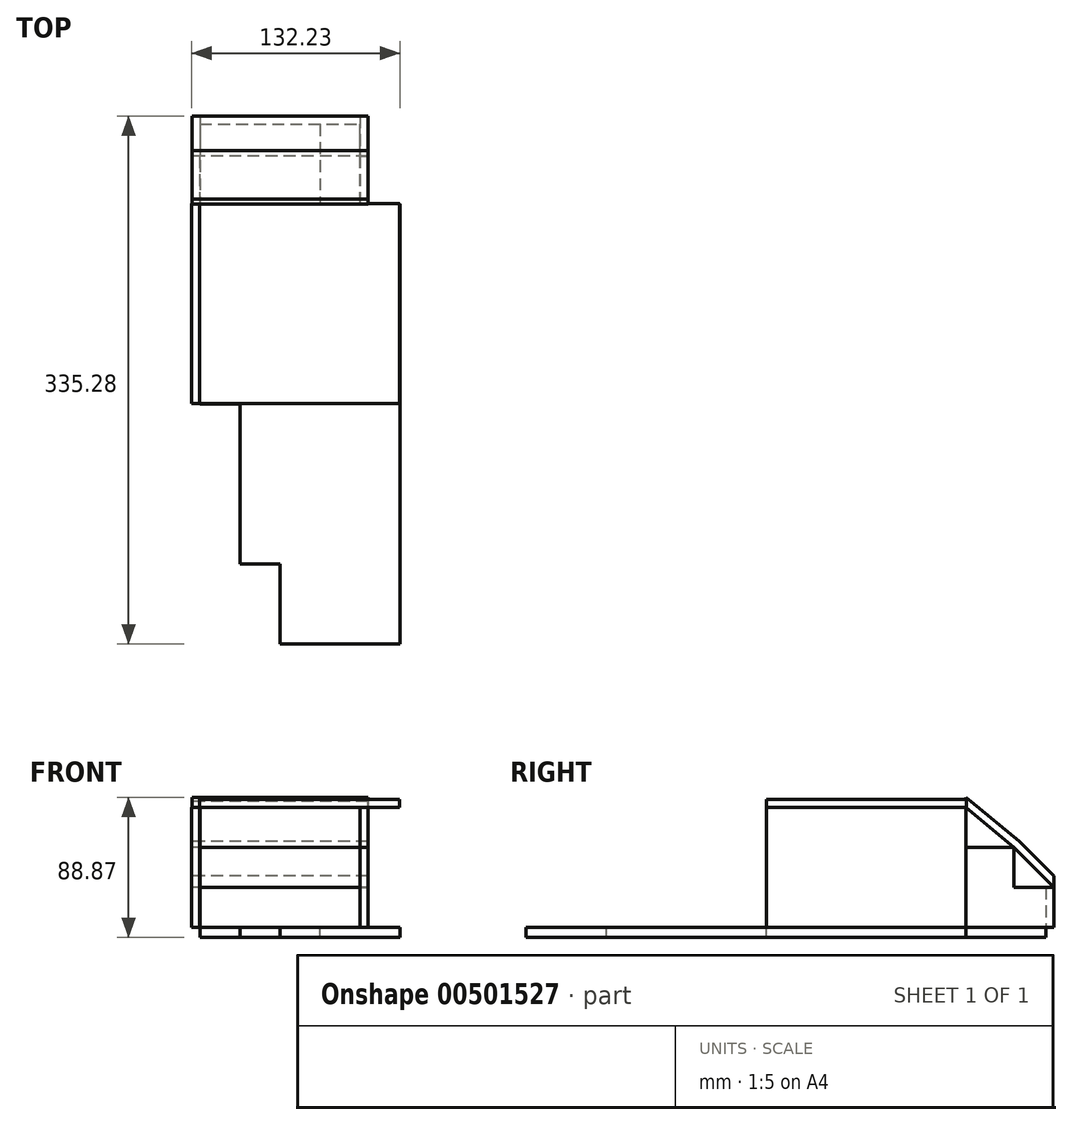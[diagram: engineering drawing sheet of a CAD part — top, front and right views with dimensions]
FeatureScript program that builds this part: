
annotation { "Feature Type Name" : "Feature", "Feature Type Description" : "" }
export const myFeature = defineFeature(function(context is Context, id is Id, definition is map)
    precondition{}
    {
        {
            var Q0;
            Q0=qCreatedBy(makeId("Top.planeOp"),FACE);
            var sketch = newSketch(context, id + "F0", { "sketchPlane" : qUnion([Q0])});
            skLineSegment(sketch, "E0.left", {"start": v(-63.5, 63.5) * mm, "end": v(-63.5, -63.5) * mm});
            skLineSegment(sketch, "E0.right", {"start": v(63.5, 63.5) * mm, "end": v(63.5, -63.5) * mm});
            skPoint(sketch, "E0.middle", {"position": v(0, 0) * mm});
            skLineSegment(sketch, "E1.top", {"start": v(-63.5, 38.1) * mm, "end": v(-38.1, 38.1) * mm, "construction": true});
            skLineSegment(sketch, "E1.left", {"start": v(-63.5, 63.5) * mm, "end": v(-63.5, 38.1) * mm, "construction": true});
            skLineSegment(sketch, "E1.right", {"start": v(-38.1, 63.5) * mm, "end": v(-38.1, 38.1) * mm, "construction": true});
            skLineSegment(sketch, "E2.0", {"start": v(-12.7, 63.5) * mm, "end": v(-12.7, 38.1) * mm, "construction": true});
            skLineSegment(sketch, "E3.0", {"start": v(12.7, 63.5) * mm, "end": v(12.7, 38.1) * mm, "construction": true});
            skLineSegment(sketch, "E4.0", {"start": v(38.1, 63.5) * mm, "end": v(38.1, 38.1) * mm, "construction": true});
            skLineSegment(sketch, "E5", {"start": v(-38.1, 38.1) * mm, "end": v(-12.7, 38.1) * mm, "construction": true});
            skLineSegment(sketch, "E6", {"start": v(12.7, 38.1) * mm, "end": v(-12.7, 38.1) * mm, "construction": true});
            skLineSegment(sketch, "E7", {"start": v(12.7, 38.1) * mm, "end": v(38.1, 38.1) * mm, "construction": true});
            skLineSegment(sketch, "E8", {"start": v(38.1, 38.1) * mm, "end": v(63.5, 38.1) * mm, "construction": true});
            skLineSegment(sketch, "E9.0", {"start": v(38.1, 12.7) * mm, "end": v(63.5, 12.7) * mm, "construction": true});
            skLineSegment(sketch, "E10.0", {"start": v(38.1, -12.7) * mm, "end": v(63.5, -12.7) * mm, "construction": true});
            skLineSegment(sketch, "E11.0", {"start": v(38.1, -38.1) * mm, "end": v(63.5, -38.1) * mm, "construction": true});
            skLineSegment(sketch, "E12.0", {"start": v(38.1, -63.5) * mm, "end": v(63.5, -63.5) * mm, "construction": true});
            skLineSegment(sketch, "E13", {"start": v(38.1, -63.5) * mm, "end": v(38.1, -38.1) * mm, "construction": true});
            skLineSegment(sketch, "E14", {"start": v(38.1, -12.7) * mm, "end": v(38.1, -38.1) * mm, "construction": true});
            skLineSegment(sketch, "E15", {"start": v(38.1, -12.7) * mm, "end": v(38.1, 12.7) * mm, "construction": true});
            skLineSegment(sketch, "E16", {"start": v(38.1, 38.1) * mm, "end": v(38.1, 12.7) * mm, "construction": true});
            skLineSegment(sketch, "E17.0", {"start": v(-63.5, 88.9) * mm, "end": v(-38.1, 88.9) * mm, "construction": true});
            skLineSegment(sketch, "E18.0", {"start": v(-63.5, 114.3) * mm, "end": v(-38.1, 114.3) * mm});
            skLineSegment(sketch, "E19", {"start": v(-63.5, 114.3) * mm, "end": v(-63.5, 63.5) * mm});
            skLineSegment(sketch, "E20", {"start": v(38.1, 63.5) * mm, "end": v(38.1, 88.9) * mm});
            skLineSegment(sketch, "E21", {"start": v(38.1, 88.9) * mm, "end": v(-38.1, 88.9) * mm, "construction": true});
            skLineSegment(sketch, "E22", {"start": v(-38.1, 114.3) * mm, "end": v(-38.1, 88.9) * mm, "construction": true});
            skLineSegment(sketch, "E23", {"start": v(-38.1, 63.5) * mm, "end": v(-38.1, 88.9) * mm, "construction": true});
            skLineSegment(sketch, "E24", {"start": v(38.1, 88.9) * mm, "end": v(38.1, 114.3) * mm});
            skLineSegment(sketch, "E25", {"start": v(38.1, 114.3) * mm, "end": v(-38.1, 114.3) * mm});
            skLineSegment(sketch, "E26.0", {"start": v(-12.7, 114.3) * mm, "end": v(-12.7, 88.9) * mm, "construction": true});
            skLineSegment(sketch, "E27.0", {"start": v(12.7, 114.3) * mm, "end": v(12.7, 88.9) * mm, "construction": true});
            skLineSegment(sketch, "E28.0", {"start": v(-12.7, 63.5) * mm, "end": v(-12.7, 88.9) * mm, "construction": true});
            skLineSegment(sketch, "E29.0", {"start": v(12.7, 63.5) * mm, "end": v(12.7, 88.9) * mm, "construction": true});
            skLineSegment(sketch, "E30.0", {"start": v(12.7, -63.5) * mm, "end": v(12.7, -38.1) * mm, "construction": true});
            skLineSegment(sketch, "E31.0", {"start": v(-12.7, -63.5) * mm, "end": v(-12.7, -38.1) * mm, "construction": true});
            skLineSegment(sketch, "E32.0", {"start": v(-38.1, -63.5) * mm, "end": v(-38.1, -38.1) * mm, "construction": true});
            skLineSegment(sketch, "E33", {"start": v(-63.5, -38.1) * mm, "end": v(-38.1, -38.1) * mm, "construction": true});
            skLineSegment(sketch, "E34", {"start": v(-12.7, -38.1) * mm, "end": v(38.1, -38.1) * mm, "construction": true});
            skLineSegment(sketch, "E35", {"start": v(-12.7, -38.1) * mm, "end": v(-38.1, -38.1) * mm, "construction": true});
            skLineSegment(sketch, "E36", {"start": v(-38.1, -63.5) * mm, "end": v(-38.1, -88.9) * mm});
            skLineSegment(sketch, "E37", {"start": v(-38.1, -88.9) * mm, "end": v(63.5, -88.9) * mm, "construction": true});
            skLineSegment(sketch, "E38", {"start": v(63.5, -88.9) * mm, "end": v(63.5, -63.5) * mm});
            skLineSegment(sketch, "E39", {"start": v(38.1, -63.5) * mm, "end": v(38.1, -88.9) * mm, "construction": true});
            skLineSegment(sketch, "E40", {"start": v(12.7, -63.5) * mm, "end": v(12.7, -88.9) * mm});
            skLineSegment(sketch, "E41", {"start": v(-12.7, -63.5) * mm, "end": v(-12.7, -88.9) * mm});
            skLineSegment(sketch, "E42", {"start": v(-38.1, -88.9) * mm, "end": v(-38.1, -165.1) * mm});
            skLineSegment(sketch, "E43", {"start": v(-38.1, -165.1) * mm, "end": v(63.5, -165.1) * mm});
            skLineSegment(sketch, "E44", {"start": v(63.5, -165.1) * mm, "end": v(63.5, -88.9) * mm});
            skLineSegment(sketch, "E45", {"start": v(-38.1, -165.1) * mm, "end": v(-38.1, -139.7) * mm, "construction": true});
            skLineSegment(sketch, "E46", {"start": v(-38.1, -139.7) * mm, "end": v(63.5, -139.7) * mm, "construction": true});
            skLineSegment(sketch, "E47", {"start": v(38.1, -88.9) * mm, "end": v(38.1, -165.1) * mm, "construction": true});
            skLineSegment(sketch, "E48", {"start": v(12.7, -88.9) * mm, "end": v(12.7, -165.1) * mm, "construction": true});
            skLineSegment(sketch, "E49", {"start": v(-12.7, -91.63) * mm, "end": v(-12.7, -165.1) * mm, "construction": true});
            skLineSegment(sketch, "E50", {"start": v(-38.1, -88.9) * mm, "end": v(-38.1, -114.3) * mm});
            skLineSegment(sketch, "E51", {"start": v(63.5, -114.3) * mm, "end": v(-38.1, -114.3) * mm, "construction": true});
            skLineSegment(sketch, "E52", {"start": v(-12.7, -165.1) * mm, "end": v(-12.7, -190.5) * mm});
            skLineSegment(sketch, "E53", {"start": v(-12.7, -190.5) * mm, "end": v(-12.7, -215.9) * mm});
            skLineSegment(sketch, "E54", {"start": v(-12.7, -215.9) * mm, "end": v(63.5, -215.9) * mm});
            skLineSegment(sketch, "E55", {"start": v(63.5, -215.9) * mm, "end": v(63.5, -165.1) * mm});
            skLineSegment(sketch, "E56", {"start": v(38.1, -165.1) * mm, "end": v(38.1, -215.9) * mm, "construction": true});
            skLineSegment(sketch, "E57", {"start": v(12.7, -165.1) * mm, "end": v(12.7, -215.9) * mm, "construction": true});
            skLineSegment(sketch, "E58", {"start": v(-12.7, -190.5) * mm, "end": v(63.5, -190.5) * mm, "construction": true});
            skLineSegment(sketch, "E59", {"start": v(12.7, 38.1) * mm, "end": v(12.7, -38.1) * mm, "construction": true});
            skLineSegment(sketch, "E60", {"start": v(-12.7, -38.1) * mm, "end": v(-12.7, 38.1) * mm, "construction": true});
            skLineSegment(sketch, "E61", {"start": v(-38.1, 38.1) * mm, "end": v(-38.1, -38.1) * mm, "construction": true});
            skLineSegment(sketch, "E62", {"start": v(38.1, -12.7) * mm, "end": v(-63.5, -12.7) * mm, "construction": true});
            skLineSegment(sketch, "E63", {"start": v(38.1, 12.7) * mm, "end": v(-63.5, 12.7) * mm, "construction": true});
            skLineSegment(sketch, "E64", {"start": v(-63.5, 63.5) * mm, "end": v(38.1, 63.5) * mm});
            skLineSegment(sketch, "E65", {"start": v(38.1, 63.5) * mm, "end": v(63.5, 63.5) * mm});
            skLineSegment(sketch, "E66", {"start": v(-63.5, -63.5) * mm, "end": v(63.5, -63.5) * mm});
            skSolve(sketch);
        }
        {
            var Q0;
            Q0=makeQuery(id+"F0.imprint","IMPRINT",FACE,{"disambiguationData":[TD([[makeQuery(id+"F0.imprint","IMPRINT",EDGE,{"derivedFrom":sQuery(id+"F0.wireOp",EDGE,"E18.0")}),-1.0]])]});
            extrude(context, id + "F1", {"entities" : qUnion([Q0]), "depth" : 6.35 * mm});
        }
        {
            var Q0;
            {var subQ3=sQuery(id+"F0.wireOp",EDGE,"E0.left");Q0=makeQuery(id+"F0.imprint","IMPRINT",FACE,{"disambiguationData":[TD([[makeQuery(id+"F0.imprint","IMPRINT",EDGE,{"derivedFrom":subQ3}),1.0]])]});}
            extrude(context, id + "F2", {"entities" : qUnion([Q0]), "operationType" : NewBodyOperationType.ADD, "depth" : 6.35 * mm});
        }
        {
            var Q0;
            {var subQ4=sQuery(id+"F0.wireOp",EDGE,"E36");Q0=makeQuery(id+"F0.imprint","IMPRINT",FACE,{"disambiguationData":[TD([[makeQuery(id+"F0.imprint","IMPRINT",EDGE,{"derivedFrom":subQ4}),1.0]])]});}
            extrude(context, id + "F3", {"entities" : qUnion([Q0]), "operationType" : NewBodyOperationType.ADD, "depth" : 6.35 * mm});
        }
        {
            var Q0;
            {var subQ0=sQuery(id+"F0.wireOp",EDGE,"E52");Q0=makeQuery(id+"F0.imprint","IMPRINT",FACE,{"disambiguationData":[TD([[makeQuery(id+"F0.imprint","IMPRINT",EDGE,{"derivedFrom":subQ0}),1.0]])]});}
            extrude(context, id + "F4", {"entities" : qUnion([Q0]), "operationType" : NewBodyOperationType.ADD, "depth" : 6.35 * mm});
        }
        {
            var Q0;
            {var subQ0=sQuery(id+"F0.wireOp",EDGE,"E43");var subQ1=sQuery(id+"F0.wireOp",EDGE,"E66");var subQ2=sQuery(id+"F0.wireOp",EDGE,"E64");Q0=makeQuery(id+"F4.boolean.opBoolean","MERGE",FACE,{"derivedFrom":[makeQuery(id+"F3.boolean.opBoolean","MERGE",FACE,{"derivedFrom":[makeQuery(id+"F2.boolean.opBoolean","MERGE",FACE,{"derivedFrom":[makeQuery(id+"F1.opExtrude","CAP_FACE",FACE,{"disambiguationData":[OSD([sQuery(id+"F0.wireOp",EDGE,"E18.0"),sQuery(id+"F0.wireOp",EDGE,"E19"),sQuery(id+"F0.wireOp",EDGE,"E20"),sQuery(id+"F0.wireOp",EDGE,"E24"),sQuery(id+"F0.wireOp",EDGE,"E25"),subQ2])],"isStart":false}),makeQuery(id+"F2.opExtrude","CAP_FACE",FACE,{"disambiguationData":[OSD([sQuery(id+"F0.wireOp",EDGE,"E0.left"),sQuery(id+"F0.wireOp",EDGE,"E0.right"),subQ2,sQuery(id+"F0.wireOp",EDGE,"E65"),subQ1])],"isStart":false})]}),makeQuery(id+"F3.opExtrude","CAP_FACE",FACE,{"disambiguationData":[OSD([sQuery(id+"F0.wireOp",EDGE,"E36"),sQuery(id+"F0.wireOp",EDGE,"E38"),sQuery(id+"F0.wireOp",EDGE,"E42"),subQ0,sQuery(id+"F0.wireOp",EDGE,"E44"),sQuery(id+"F0.wireOp",EDGE,"E50"),subQ1])],"isStart":false})]}),makeQuery(id+"F4.opExtrude","CAP_FACE",FACE,{"disambiguationData":[OSD([subQ0,sQuery(id+"F0.wireOp",EDGE,"E52"),sQuery(id+"F0.wireOp",EDGE,"E53"),sQuery(id+"F0.wireOp",EDGE,"E54"),sQuery(id+"F0.wireOp",EDGE,"E55")])],"isStart":false})]});}
            var sketch = newSketch(context, id + "F5", { "sketchPlane" : qUnion([Q0])});
            skLineSegment(sketch, "E67", {"start": v(-63.5, 114.3) * mm, "end": v(38.1, 114.3) * mm});
            skLineSegment(sketch, "E68", {"start": v(38.1, 114.3) * mm, "end": v(38.1, 63.5) * mm});
            skLineSegment(sketch, "E69", {"start": v(38.1, 63.5) * mm, "end": v(-63.5, 63.5) * mm});
            skLineSegment(sketch, "E70", {"start": v(-63.5, 63.5) * mm, "end": v(-63.5, 114.3) * mm});
            skLineSegment(sketch, "E71", {"start": v(38.1, 114.3) * mm, "end": v(12.7, 114.3) * mm, "construction": true});
            skLineSegment(sketch, "E72", {"start": v(12.7, 114.3) * mm, "end": v(12.7, 88.9) * mm});
            skLineSegment(sketch, "E73", {"start": v(12.7, 88.9) * mm, "end": v(12.7, 63.5) * mm});
            skLineSegment(sketch, "E74", {"start": v(12.7, 88.9) * mm, "end": v(38.1, 88.9) * mm});
            skLineSegment(sketch, "E75.0", {"start": v(43.18, 119.38) * mm, "end": v(43.18, 63.5) * mm});
            skLineSegment(sketch, "E75.1", {"start": v(-68.58, 119.38) * mm, "end": v(43.18, 119.38) * mm});
            skLineSegment(sketch, "E75.2", {"start": v(-68.58, 63.5) * mm, "end": v(-68.58, 119.38) * mm});
            skLineSegment(sketch, "E76", {"start": v(38.1, 63.5) * mm, "end": v(43.18, 63.5) * mm});
            skLineSegment(sketch, "E77", {"start": v(-63.5, 63.5) * mm, "end": v(-68.58, 63.5) * mm});
            skSolve(sketch);
        }
        {
            var Q0;
            {var subQ5=sQuery(id+"F5.wireOp",EDGE,"E70");Q0=makeQuery(id+"F5.imprint","IMPRINT",FACE,{"disambiguationData":[TD([[makeQuery(id+"F5.imprint","IMPRINT",EDGE,{"derivedFrom":subQ5}),-1.0]])]});}
            extrude(context, id + "F6", {"entities" : qUnion([Q0]), "depth" : 50.8 * mm});
        }
        {
            var Q0;
            {var subQ3=sQuery(id+"F5.wireOp",EDGE,"E72");Q0=makeQuery(id+"F5.imprint","IMPRINT",FACE,{"disambiguationData":[TD([[makeQuery(id+"F5.imprint","IMPRINT",EDGE,{"derivedFrom":subQ3}),1.0]])]});}
            var Q1;
            {var subQ4=sQuery(id+"F5.wireOp",EDGE,"E73");Q1=makeQuery(id+"F5.imprint","IMPRINT",FACE,{"disambiguationData":[TD([[makeQuery(id+"F5.imprint","IMPRINT",EDGE,{"derivedFrom":subQ4}),1.0]])]});}
            extrude(context, id + "F7", {"entities" : qUnion([Q0, Q1]), "operationType" : NewBodyOperationType.REMOVE, "oppositeDirection" : true, "depth" : 25.4 * mm});
        }
        {
            var Q0;
            {var subQ3=sQuery(id+"F5.wireOp",EDGE,"E76");Q0=makeQuery(id+"F5.imprint","IMPRINT",FACE,{"disambiguationData":[TD([[makeQuery(id+"F5.imprint","IMPRINT",EDGE,{"derivedFrom":subQ3}),-1.0]])]});}
            var sketch = newSketch(context, id + "F8", { "sketchPlane" : qUnion([Q0])});
            skLineSegment(sketch, "E78", {"start": v(-63.65, 63.74) * mm, "end": v(-63.65, -63.1) * mm});
            skLineSegment(sketch, "E79", {"start": v(-63.65, -63.1) * mm, "end": v(-38.28, -63.1) * mm});
            skLineSegment(sketch, "E80", {"start": v(-63.65, 63.74) * mm, "end": v(63.35, 63.74) * mm});
            skLineSegment(sketch, "E81", {"start": v(63.35, 63.74) * mm, "end": v(63.35, -63.26) * mm});
            skLineSegment(sketch, "E82", {"start": v(63.35, -63.26) * mm, "end": v(-38.28, -63.1) * mm});
            skLineSegment(sketch, "E83", {"start": v(37.95, 63.74) * mm, "end": v(63.35, 63.74) * mm});
            skLineSegment(sketch, "E84.0", {"start": v(-68.73, 63.74) * mm, "end": v(-68.73, -63.1) * mm});
            skLineSegment(sketch, "E85.0", {"start": v(68.43, 68.82) * mm, "end": v(68.43, -63.26) * mm});
            skLineSegment(sketch, "E85.1", {"start": v(43.03, 68.82) * mm, "end": v(68.43, 68.82) * mm});
            skLineSegment(sketch, "E86", {"start": v(37.95, 63.74) * mm, "end": v(37.95, 68.82) * mm});
            skLineSegment(sketch, "E87", {"start": v(37.95, 68.82) * mm, "end": v(43.03, 68.82) * mm});
            skLineSegment(sketch, "E88", {"start": v(-68.73, 63.74) * mm, "end": v(-63.65, 63.74) * mm});
            skLineSegment(sketch, "E89", {"start": v(-68.73, -63.1) * mm, "end": v(-63.65, -63.1) * mm});
            skLineSegment(sketch, "E90", {"start": v(63.35, -63.26) * mm, "end": v(68.43, -63.26) * mm});
            skSolve(sketch);
        }
        {
            var Q0;
            {var subQ0=sQuery(id+"F8.wireOp",EDGE,"E83");Q0=makeQuery(id+"F8.imprint","IMPRINT",FACE,{"disambiguationData":[TD([[makeQuery(id+"F8.imprint","IMPRINT",EDGE,{"derivedFrom":subQ0}),1.0]])]});}
            var Q1;
            Q1=makeQuery(id+"F8.imprint","IMPRINT",FACE,{"disambiguationData":[TD([[makeQuery(id+"F8.imprint","IMPRINT",EDGE,{"derivedFrom":sQuery(id+"F8.wireOp",EDGE,"E78")}),-1.0]])]});
            extrude(context, id + "F9", {"entities" : qUnion([Q0, Q1]), "depth" : 76.2 * mm});
        }
        {
            var Q0;
            Q0=makeQuery(id+"F6.opExtrude","SWEPT_FACE",FACE,{"disambiguationData":[OSD([sQuery(id+"F5.wireOp",EDGE,"E75.2")])]});
            var sketch = newSketch(context, id + "F10", { "sketchPlane" : qUnion([Q0])});
            skLineSegment(sketch, "E91", {"start": v(-119.38, 57.15) * mm, "end": v(-93.98, 57.15) * mm});
            skLineSegment(sketch, "E92", {"start": v(-93.98, 57.15) * mm, "end": v(-93.98, 31.75) * mm});
            skLineSegment(sketch, "E93", {"start": v(-93.98, 31.75) * mm, "end": v(-119.38, 31.75) * mm});
            skLineSegment(sketch, "E94", {"start": v(-119.38, 31.75) * mm, "end": v(-119.38, 57.15) * mm});
            skSolve(sketch);
        }
        {
            var Q0;
            Q0=makeQuery(id+"F10.imprint","IMPRINT",FACE,{"disambiguationData":[TD([[makeQuery(id+"F10.imprint","IMPRINT",EDGE,{"derivedFrom":sQuery(id+"F10.wireOp",EDGE,"E91")}),1.0]])]});
            extrude(context, id + "F11", {"entities" : qUnion([Q0]), "operationType" : NewBodyOperationType.REMOVE, "oppositeDirection" : true, "depth" : 114.3 * mm});
        }
        {
            var Q0;
            Q0=makeQuery(id+"F6.opExtrude","SWEPT_FACE",FACE,{"disambiguationData":[OSD([sQuery(id+"F5.wireOp",EDGE,"E75.2")])]});
            var sketch = newSketch(context, id + "F12", { "sketchPlane" : qUnion([Q0])});
            skLineSegment(sketch, "E95", {"start": v(-93.98, 57.15) * mm, "end": v(-63.5, 57.15) * mm});
            skLineSegment(sketch, "E96", {"start": v(-63.5, 57.15) * mm, "end": v(-63.5, 82.55) * mm});
            skLineSegment(sketch, "E97", {"start": v(-63.5, 82.55) * mm, "end": v(-93.98, 57.15) * mm});
            skLineSegment(sketch, "E98", {"start": v(-93.98, 57.15) * mm, "end": v(-93.98, 31.75) * mm});
            skLineSegment(sketch, "E99", {"start": v(-93.98, 31.75) * mm, "end": v(-119.38, 31.75) * mm});
            skLineSegment(sketch, "E100", {"start": v(-119.38, 31.75) * mm, "end": v(-93.98, 57.15) * mm});
            skLineSegment(sketch, "E101.0", {"start": v(-66.75, 86.45) * mm, "end": v(-97.4, 60.9) * mm});
            skLineSegment(sketch, "E101.1", {"start": v(-119.38, 38.93) * mm, "end": v(-97.4, 60.9) * mm});
            skLineSegment(sketch, "E102", {"start": v(-63.5, 82.55) * mm, "end": v(-63.5, 88.87) * mm});
            skLineSegment(sketch, "E103", {"start": v(-66.75, 86.45) * mm, "end": v(-63.5, 88.87) * mm});
            skLineSegment(sketch, "E104", {"start": v(-119.38, 31.75) * mm, "end": v(-119.38, 38.93) * mm});
            skSolve(sketch);
        }
        {
            var Q0;
            Q0=makeQuery(id+"F12.imprint","IMPRINT",FACE,{"disambiguationData":[TD([[makeQuery(id+"F12.imprint","IMPRINT",EDGE,{"derivedFrom":sQuery(id+"F12.wireOp",EDGE,"E98")}),-1.0]])]});
            var Q1;
            Q1=makeQuery(id+"F12.imprint","IMPRINT",FACE,{"disambiguationData":[TD([[makeQuery(id+"F12.imprint","IMPRINT",EDGE,{"derivedFrom":sQuery(id+"F12.wireOp",EDGE,"E95")}),-1.0]])]});
            extrude(context, id + "F13", {"entities" : qUnion([Q0, Q1]), "oppositeDirection" : true, "depth" : 5.08 * mm});
        }
        {
            var Q0;
            Q0=makeQuery(id+"F12.imprint","IMPRINT",FACE,{"disambiguationData":[TD([[makeQuery(id+"F12.imprint","IMPRINT",EDGE,{"derivedFrom":sQuery(id+"F12.wireOp",EDGE,"E97")}),-1.0]])]});
            extrude(context, id + "F14", {"entities" : qUnion([Q0]), "oppositeDirection" : true, "depth" : 111.76 * mm});
        }
        {
            var Q0;
            Q0=makeQuery(id+"F6.opExtrude","SWEPT_FACE",FACE,{"disambiguationData":[OSD([sQuery(id+"F5.wireOp",EDGE,"E75.0")])]});
            var sketch = newSketch(context, id + "F15", { "sketchPlane" : qUnion([Q0])});
            skLineSegment(sketch, "E105", {"start": v(93.98, 57.15) * mm, "end": v(63.5, 57.15) * mm});
            skLineSegment(sketch, "E106", {"start": v(63.5, 57.15) * mm, "end": v(63.5, 82.55) * mm});
            skLineSegment(sketch, "E107", {"start": v(63.5, 82.55) * mm, "end": v(93.98, 57.15) * mm});
            skLineSegment(sketch, "E108", {"start": v(93.98, 57.15) * mm, "end": v(93.98, 31.75) * mm});
            skLineSegment(sketch, "E109", {"start": v(93.98, 31.75) * mm, "end": v(119.38, 31.75) * mm});
            skLineSegment(sketch, "E110", {"start": v(119.38, 31.75) * mm, "end": v(93.98, 57.15) * mm});
            skSolve(sketch);
        }
        {
            var Q0;
            Q0=makeQuery(id+"F15.imprint","IMPRINT",FACE,{"disambiguationData":[TD([[makeQuery(id+"F15.imprint","IMPRINT",EDGE,{"derivedFrom":sQuery(id+"F15.wireOp",EDGE,"E105")}),-1.0]])]});
            var Q1;
            Q1=makeQuery(id+"F15.imprint","IMPRINT",FACE,{"disambiguationData":[TD([[makeQuery(id+"F15.imprint","IMPRINT",EDGE,{"derivedFrom":sQuery(id+"F15.wireOp",EDGE,"E108")}),-1.0]])]});
            extrude(context, id + "F16", {"entities" : qUnion([Q0, Q1]), "oppositeDirection" : true, "depth" : 5.08 * mm});
        }
        {
            var Q0;
            Q0=makeQuery(id+"F9.opExtrude","SWEPT_FACE",FACE,{"disambiguationData":[OSD([sQuery(id+"F8.wireOp",EDGE,"E89")])]});
            var sketch = newSketch(context, id + "F17", { "sketchPlane" : qUnion([Q0])});
            skLineSegment(sketch, "E111", {"start": v(-63.65, 82.55) * mm, "end": v(63.35, 82.55) * mm});
            skLineSegment(sketch, "E112", {"start": v(63.35, 82.55) * mm, "end": v(63.35, 87.63) * mm});
            skLineSegment(sketch, "E113", {"start": v(63.35, 87.63) * mm, "end": v(-63.65, 87.63) * mm});
            skLineSegment(sketch, "E114", {"start": v(-63.65, 87.63) * mm, "end": v(-63.65, 82.55) * mm});
            skSolve(sketch);
        }
        {
            var Q0;
            Q0=makeQuery(id+"F17.imprint","IMPRINT",FACE,{"disambiguationData":[TD([[makeQuery(id+"F17.imprint","IMPRINT",EDGE,{"derivedFrom":sQuery(id+"F17.wireOp",EDGE,"E111")}),1.0]])]});
            extrude(context, id + "F18", {"entities" : qUnion([Q0]), "oppositeDirection" : true, "depth" : 127 * mm});
        }
    });
